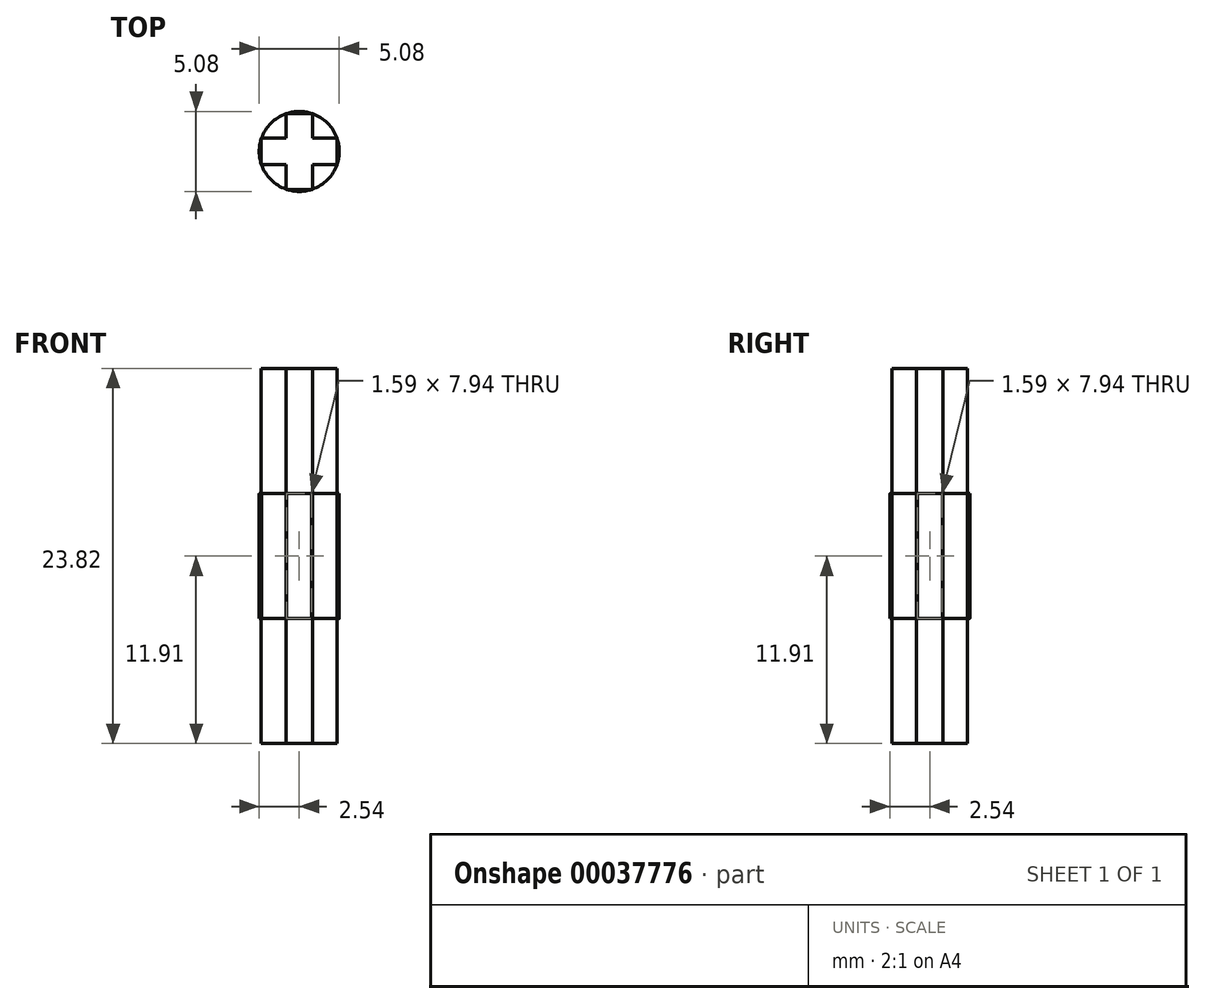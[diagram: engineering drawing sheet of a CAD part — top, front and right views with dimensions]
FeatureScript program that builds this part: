
annotation { "Feature Type Name" : "Feature", "Feature Type Description" : "" }
export const myFeature = defineFeature(function(context is Context, id is Id, definition is map)
    precondition{}
    {
        {
            var Q0;
            Q0=qCreatedBy(makeId("Top.planeOp"),FACE);
            var sketch = newSketch(context, id + "F0", { "sketchPlane" : qUnion([Q0])});
            skCircle(sketch, "E0", {"center": v(0, 0) * mm, "radius": 2.54 * mm});
            skSolve(sketch);
        }
        {
            var Q0;
            Q0 = qSketchRegion(id + "F0", true);
            extrude(context, id + "F1", {"entities" : qUnion([Q0]), "endBound" : BoundingType.SYMMETRIC, "depth" : 7.94 * mm});
        }
        {
            var Q0;
            Q0=qCreatedBy(makeId("Top.planeOp"),FACE);
            var sketch = newSketch(context, id + "F2", { "sketchPlane" : qUnion([Q0])});
            skLineSegment(sketch, "E1.rect.bottom", {"start": v(0.84, 2.41) * mm, "end": v(-0.84, 2.41) * mm});
            skLineSegment(sketch, "E1.rect.top", {"start": v(0.84, -2.41) * mm, "end": v(-0.84, -2.41) * mm});
            skLineSegment(sketch, "E1.rect.left", {"start": v(0.84, 2.41) * mm, "end": v(0.84, -2.41) * mm});
            skLineSegment(sketch, "E1.rect.right", {"start": v(-0.84, 2.41) * mm, "end": v(-0.84, -2.41) * mm});
            skPoint(sketch, "E1.rect.middle", {"position": v(0, 0) * mm});
            skLineSegment(sketch, "E2.rect.bottom", {"start": v(2.41, -0.84) * mm, "end": v(-2.41, -0.84) * mm});
            skLineSegment(sketch, "E2.rect.top", {"start": v(2.41, 0.84) * mm, "end": v(-2.41, 0.84) * mm});
            skLineSegment(sketch, "E2.rect.left", {"start": v(2.41, -0.84) * mm, "end": v(2.41, 0.84) * mm});
            skLineSegment(sketch, "E2.rect.right", {"start": v(-2.41, -0.84) * mm, "end": v(-2.41, 0.84) * mm});
            skSolve(sketch);
        }
        {
            var Q0;
            Q0 = qSketchRegion(id + "F2", true);
            extrude(context, id + "F3", {"entities" : qUnion([Q0]), "operationType" : NewBodyOperationType.ADD, "endBound" : BoundingType.SYMMETRIC, "depth" : 23.8 * mm});
        }
    });
